# Revit family: LEGRAND_NON INTERLOCKED SOCKETS_SURFACE MOUNTED_IP44_40
name_source: partatom
category: Installations électriques
revit_build: Autodesk Revit 2018 (Build: 20170223_1515(x64)
units: mm (PartAtom-declared; Revit-internal decimal feet)

## family parameters
Conserver l'orientation des annotations = Non
Cote de connecteur circulaire = Utiliser le diamètre
Couper avec des vides une fois chargée = Non
Hôte = Face
Partagée = Non
Point de calcul de pièce = Non
Type d'élément = Normal

## types (3) — shared parameters
Description = international standard socket for flush or surface mounting with accessory allows the connection of power devices
Dia bouchon = 48 mm
Elévation par défaut = 1000 mm  [stored 3.28084 ft]
Fabricant = Legrand
Flush E or Surface mounting S = flush and surface mounting
General Conditions of Use = https://export.legrand.com
Maximum installation temperature = 40°C
Maximum use temperature = 100°C
Minimum installation temperature = -20°C
Minimum use temperature = -50°C
RAY BOUCHON = 24 mm
Ray = 24 mm
Standard IEC or NFC = IEC
Tension V = 40 50 V  50/60 Hz white
characteristic color = white
connecting type = screw terminals
depth for flush mounting mm = 58 mm  [stored 0.190289 ft]
h1 = 64 mm
halogen free = Oui
height mm = 106 mm  [stored 0.347769 ft]
horizontal fixing distance mm = 52 mm
intensity A = 16 A
material of box = plastic
protection class IP = IP44
resistance to chocks IK = 09
vertical fixing distance mm = 60 mm
width mm = 74 mm  [stored 0.242782 ft]

## per-type parameters (varying)
| type | Modèle | Number of poles | Position of earth h | depth mm |
| panel mounting socket Hypra   IP44   ELV 16 A   40/50V   2P   plast surface mounting | 052403 | 2 | 12 | 105 mm  [stored 0.344488 ft] |
| panel mounting socket Hypra   IP44   ELV 16 A   40/50V   3P   plast surface mounting | 052404 | 3 | 12 | 97 mm |
| panel mounting socket Hypra   IP44   ELV 16 A   20/50 V continu   2P   plast surface mounting | 052405 | 2 | 10 | 105 mm  [stored 0.344488 ft] |

note: [stored X ft] marks values corroborated as IEEE doubles in the binary element streams (Revit-internal decimal feet)
